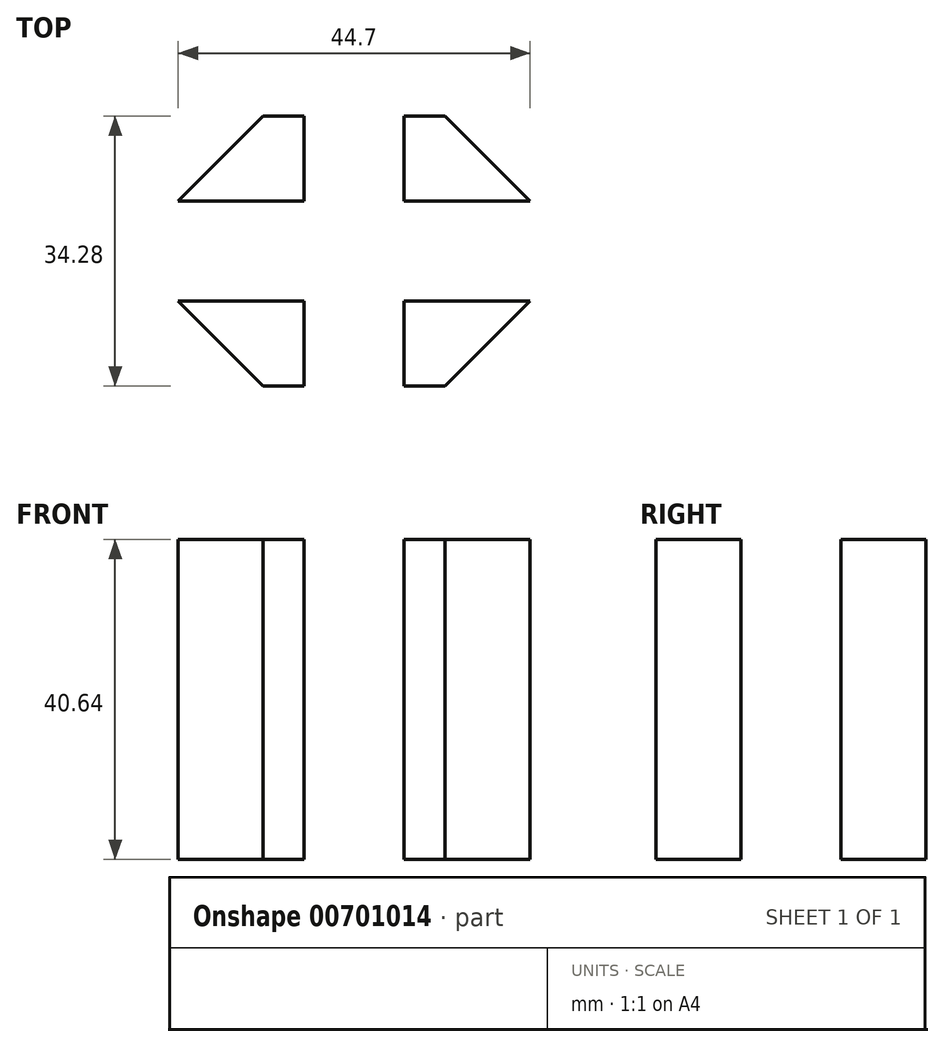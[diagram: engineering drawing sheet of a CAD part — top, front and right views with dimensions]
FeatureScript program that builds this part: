
annotation { "Feature Type Name" : "Feature", "Feature Type Description" : "" }
export const myFeature = defineFeature(function(context is Context, id is Id, definition is map)
    precondition{}
    {
        {
            var Q0;
            Q0=qCreatedBy(makeId("Top.planeOp"),FACE);
            var sketch = newSketch(context, id + "F0", { "sketchPlane" : qUnion([Q0])});
            skLineSegment(sketch, "E0", {"start": v(-22.35, 6.35) * mm, "end": v(-11.56, 17.15) * mm});
            skLineSegment(sketch, "E1", {"start": v(-11.56, 17.15) * mm, "end": v(-6.35, 17.15) * mm});
            skLineSegment(sketch, "E2", {"start": v(-6.35, 17.14) * mm, "end": v(-6.35, 6.35) * mm});
            skLineSegment(sketch, "E3", {"start": v(0, -36.84) * mm, "end": v(0, 44.12) * mm, "construction": true});
            skLineSegment(sketch, "E4.MirrorCS", {"start": v(6.35, 17.14) * mm, "end": v(6.35, 6.35) * mm});
            skLineSegment(sketch, "E5.MirrorCS", {"start": v(11.56, 17.15) * mm, "end": v(6.35, 17.15) * mm});
            skLineSegment(sketch, "E6.MirrorCS", {"start": v(22.35, 6.35) * mm, "end": v(11.56, 17.15) * mm});
            skLineSegment(sketch, "E7", {"start": v(-22.35, 6.35) * mm, "end": v(-6.35, 6.35) * mm});
            skLineSegment(sketch, "E8.MirrorCS", {"start": v(22.35, 6.35) * mm, "end": v(6.35, 6.35) * mm});
            skLineSegment(sketch, "E9", {"start": v(-55.17, 0) * mm, "end": v(63.4, 0) * mm, "construction": true});
            skLineSegment(sketch, "E10.MirrorCS", {"start": v(-22.35, -6.35) * mm, "end": v(-6.35, -6.35) * mm});
            skLineSegment(sketch, "E11.MirrorCS", {"start": v(-22.35, -6.35) * mm, "end": v(-11.56, -17.15) * mm});
            skLineSegment(sketch, "E12.MirrorCS", {"start": v(-11.56, -17.15) * mm, "end": v(-6.35, -17.15) * mm});
            skLineSegment(sketch, "E13.MirrorCS", {"start": v(-6.35, -17.14) * mm, "end": v(-6.35, -6.35) * mm});
            skLineSegment(sketch, "E14.MirrorCS", {"start": v(22.35, -6.35) * mm, "end": v(6.35, -6.35) * mm});
            skLineSegment(sketch, "E15.MirrorCS", {"start": v(6.35, -17.14) * mm, "end": v(6.35, -6.35) * mm});
            skLineSegment(sketch, "E16.MirrorCS", {"start": v(11.56, -17.15) * mm, "end": v(6.35, -17.15) * mm});
            skLineSegment(sketch, "E17.MirrorCS", {"start": v(22.35, -6.35) * mm, "end": v(11.56, -17.15) * mm});
            skLineSegment(sketch, "E18.MirrorCS", {"start": v(0, 36.84) * mm, "end": v(0, -44.12) * mm, "construction": true});
            skSolve(sketch);
        }
        {
            var Q0;
            Q0 = qSketchRegion(id + "F0", true);
            extrude(context, id + "F1", {"entities" : qUnion([Q0]), "depth" : 40.64 * mm, "offsetDistance" : 25.4 * mm});
        }
    });
